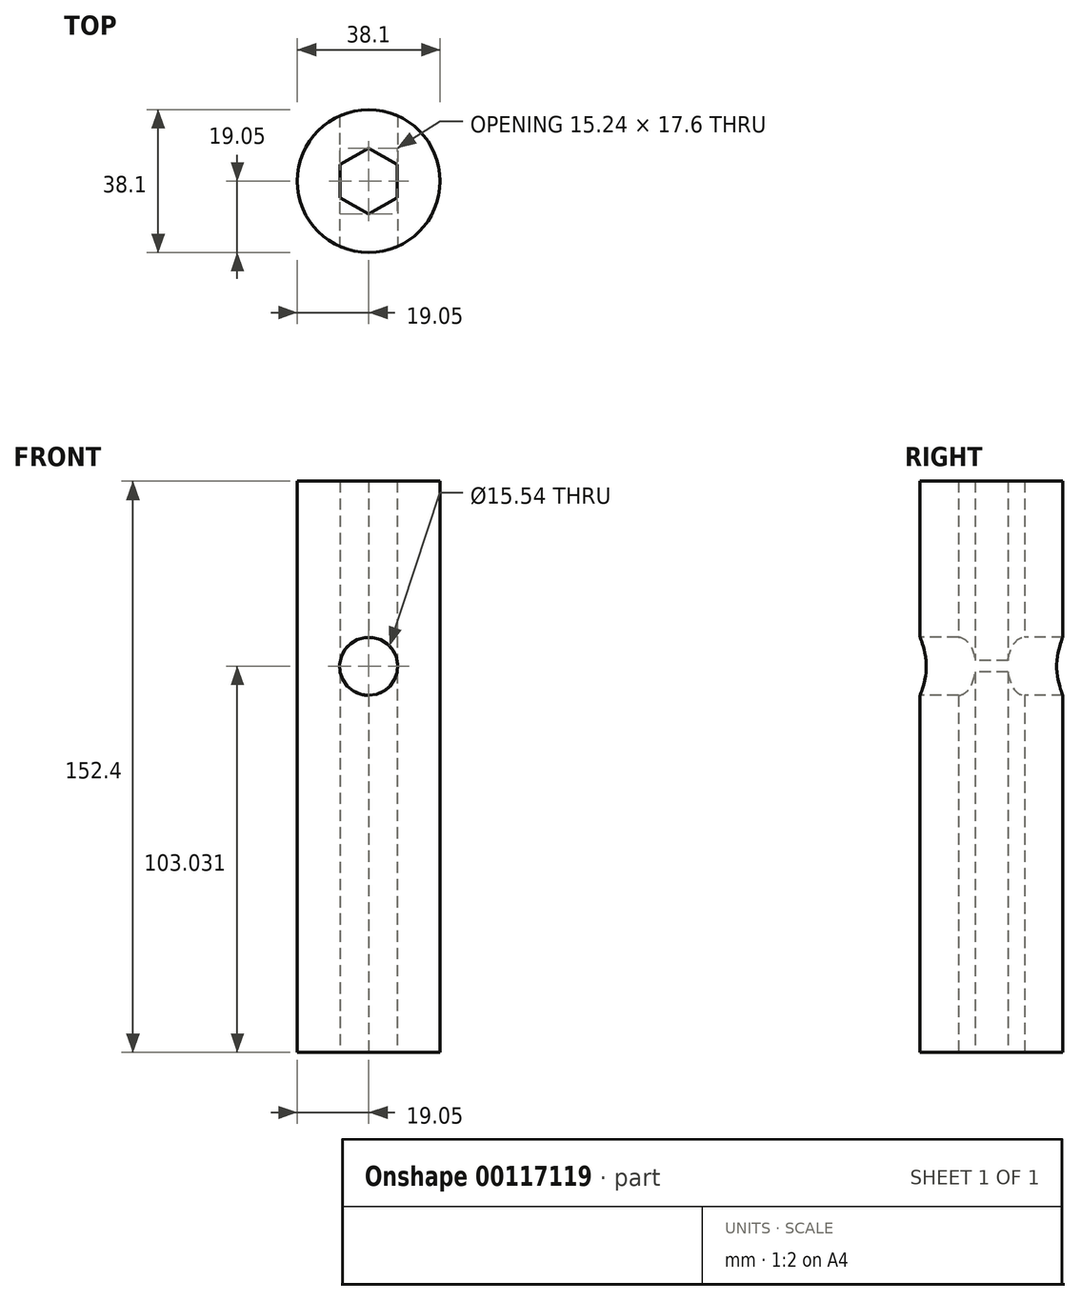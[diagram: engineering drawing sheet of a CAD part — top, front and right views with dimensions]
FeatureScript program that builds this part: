
annotation { "Feature Type Name" : "Feature", "Feature Type Description" : "" }
export const myFeature = defineFeature(function(context is Context, id is Id, definition is map)
    precondition{}
    {
        {
            var Q0;
            Q0=qCreatedBy(makeId("Top.planeOp"),FACE);
            var sketch = newSketch(context, id + "F0", { "sketchPlane" : qUnion([Q0])});
            skCircle(sketch, "E0", {"center": v(0, 0) * mm, "radius": 19.05 * mm});
            skCircle(sketch, "E1.cCircle", {"center": v(0, 0) * mm, "radius": 7.62 * mm, "construction": true});
            skLineSegment(sketch, "E1.0", {"start": v(7.62, 4.4) * mm, "end": v(7.62, -4.4) * mm});
            skLineSegment(sketch, "E1.1", {"start": v(7.62, -4.4) * mm, "end": v(0, -8.8) * mm});
            skLineSegment(sketch, "E1.2", {"start": v(0, -8.8) * mm, "end": v(-7.62, -4.4) * mm});
            skLineSegment(sketch, "E1.3", {"start": v(-7.62, -4.4) * mm, "end": v(-7.62, 4.4) * mm});
            skLineSegment(sketch, "E1.4", {"start": v(-7.62, 4.4) * mm, "end": v(0, 8.8) * mm});
            skLineSegment(sketch, "E1.5", {"start": v(0, 8.8) * mm, "end": v(7.62, 4.4) * mm});
            skPoint(sketch, "E1.0.midPoint", {"position": v(7.62, 0) * mm});
            skSolve(sketch);
        }
        {
            var Q0;
            Q0 = qSketchRegion(id + "F0", true);
            extrude(context, id + "F1", {"entities" : qUnion([Q0]), "depth" : 152.4 * mm});
        }
        {
            var Q0;
            Q0=qCreatedBy(makeId("Front.planeOp"),FACE);
            var sketch = newSketch(context, id + "F2", { "sketchPlane" : qUnion([Q0])});
            skCircle(sketch, "E2", {"center": v(0, 103.03) * mm, "radius": 7.77 * mm});
            skSolve(sketch);
        }
        {
            var Q0;
            Q0 = qSketchRegion(id + "F2", true);
            extrude(context, id + "F3", {"entities" : qUnion([Q0]), "operationType" : NewBodyOperationType.REMOVE, "endBound" : BoundingType.THROUGH_ALL, "oppositeDirection" : true, "depth" : 25.4 * mm, "hasSecondDirection" : true, "secondDirectionBound" : SecondDirectionBoundingType.THROUGH_ALL, "secondDirectionOppositeDirection" : false, "secondDirectionDepth" : 25.4 * mm});
        }
    });
